# Revit family: Bath-Alcove-Whirlpool-KOHLER-KARESS-K-76448H_1
name_source: partatom
category: Plumbing Fixtures
revit_build: Autodesk Revit 2017 (Build: 20160225_1515(x64)
units: mm (PartAtom-declared; Revit-internal decimal feet)

## family parameters
Cut with Voids When Loaded = No
Host = Face
OmniClass Number = 23.31.15.00
OmniClass Title = Bathtubs
Part Type = Normal
Room Calculation Point = No
Round Connector Dimension = Use Diameter
Shared = No

## types (1)
- 0-White
    ADA Compliant = No
    Amplifer Electrical Connector = Amplifer Electrical Connector
    Apparent Load = 1400 VA
    Assembly Code = D2010500
    Blower Electrical Connector = Blower Electrical Connector
    CW Connection = Yes
    Cold Water Inlet = Cold Water Inlet
    Date Modified = 10/12/2021
    Default Elevation = 0"
    Description = 1.7m Integrated Whirlpool Bath With Faucet And E-Drain (Left Alcove)
    Drain Included = Yes
    Electrical Connector = Yes
    Electrical Note = Dedicated Branch Circuit Required, Protected With Class A Ground-Fault Circuit-Interrupt (GFCI)
    Finish = KOHLER-Acrylic-0-White
    Flow Rate = 0 GPM
    HW Connection = Yes
    Heater Electrical Connector = Heater Electrical Connector
    Height = 32 3/16"
    Hot Water Inlet = Hot Water Inlet
    Length = 31 1/2"
    Manufacturer = KOHLER Co.
    Master Format 2014 = 22 41 19
    Master Format 2014 Name = Residential Bathtubs
    Material = Acrylic
    Model = K-76448H-NW-0
    Pressure = 0.00 psi
    Product Documentation Link = http://resources.kohler.com
    Product Name = Karess
    Product Page URL = https://www.kohlerasiapacific.com
    Pump Electrical Connector = Pump Electrical Connector
    Type = 1
    URL = https://www.kohlerasiapacific.com
    Vent Connection = No
    Voltage = 220 V
    Waste Connection = Yes
    Waste Water Outlet = Waste Water Outlet
    WaterSense Certified = No
    Width = 66 15/16"

## geometry (parser evidence)
native form markers: Sweep x4
no freeform markers — native parametric forms only
